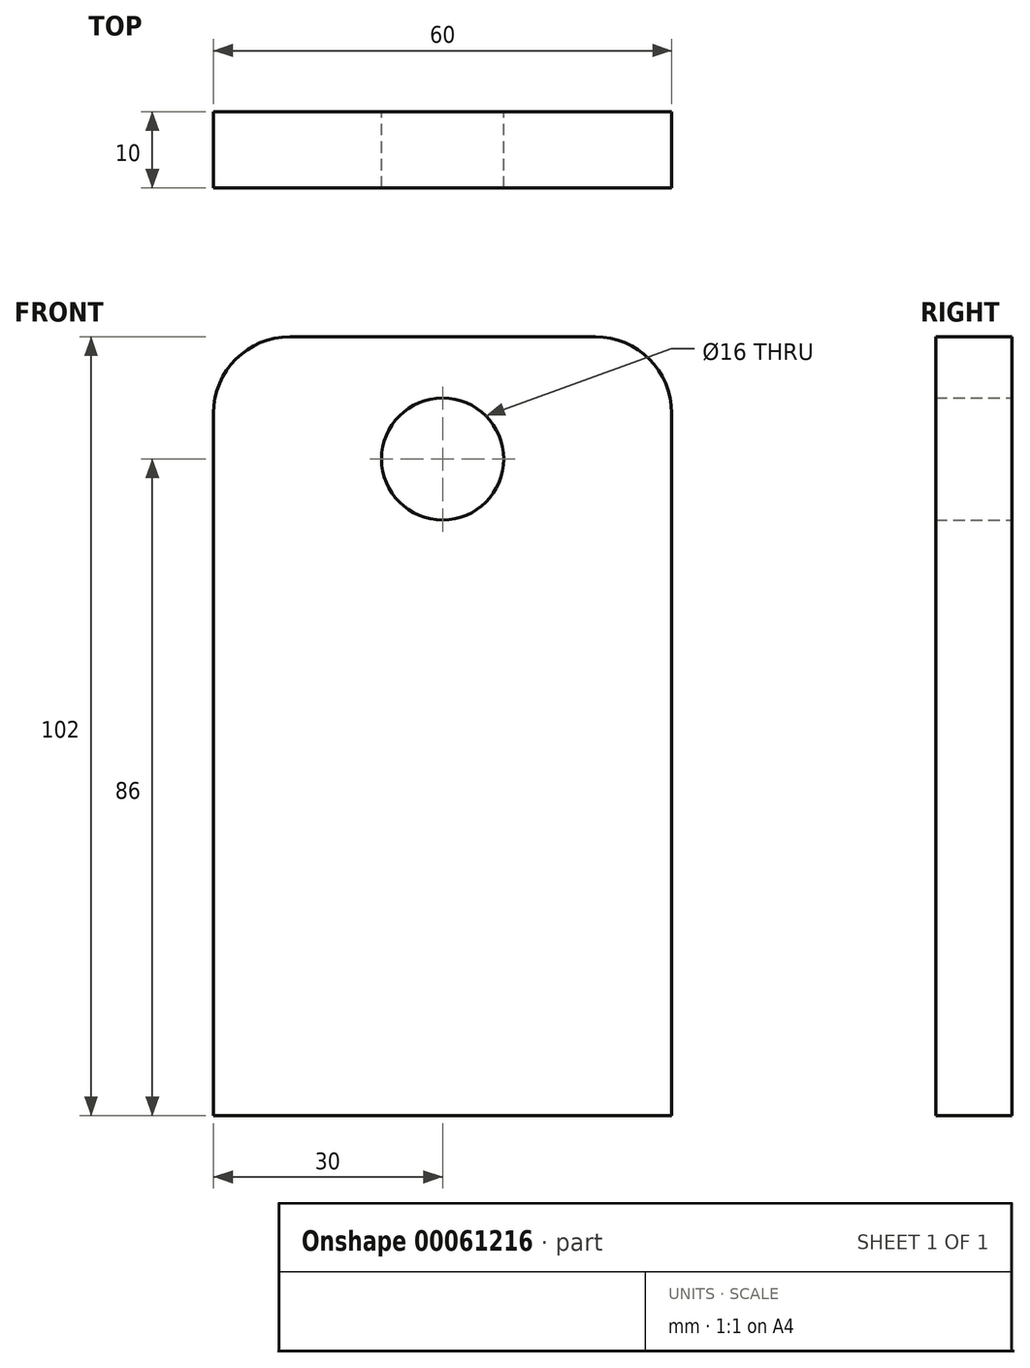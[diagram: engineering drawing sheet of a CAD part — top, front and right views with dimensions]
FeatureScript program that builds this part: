
annotation { "Feature Type Name" : "Feature", "Feature Type Description" : "" }
export const myFeature = defineFeature(function(context is Context, id is Id, definition is map)
    precondition{}
    {
        {
            var Q0;
            Q0=qCreatedBy(makeId("Front.planeOp"),FACE);
            var sketch = newSketch(context, id + "F0", { "sketchPlane" : qUnion([Q0])});
            skLineSegment(sketch, "E0.bottom", {"start": v(0, 0) * mm, "end": v(60, 0) * mm});
            skLineSegment(sketch, "E0.top", {"start": v(10, 102) * mm, "end": v(50, 102) * mm});
            skLineSegment(sketch, "E0.left", {"start": v(0, 0) * mm, "end": v(0, 92) * mm});
            skLineSegment(sketch, "E0.right", {"start": v(60, 0) * mm, "end": v(60, 92) * mm});
            skPoint(sketch, "E1.visualSharp", {"position": v(0, 102) * mm});
            skArc(sketch, "E1.filletArc", {"start": v(10, 102) * mm, "mid": v(2.93, 99.07) * mm, "end": v(0, 92) * mm});
            skPoint(sketch, "E2.visualSharp", {"position": v(60, 102) * mm});
            skArc(sketch, "E2.filletArc", {"start": v(60, 92) * mm, "mid": v(57.07, 99.07) * mm, "end": v(50, 102) * mm});
            skCircle(sketch, "E3", {"center": v(30, 86) * mm, "radius": 8 * mm});
            skPoint(sketch, "E3.centerSnap0", {"position": v(30, 0) * mm});
            skSolve(sketch);
        }
        {
            var Q0;
            Q0=makeQuery(id+"F0.imprint","IMPRINT",FACE,{"disambiguationData":[TD([[makeQuery(id+"F0.imprint","IMPRINT",EDGE,{"derivedFrom":sQuery(id+"F0.wireOp",EDGE,"E0.bottom")}),1.0]])]});
            extrude(context, id + "F1", {"entities" : qUnion([Q0]), "depth" : 10 * mm});
        }
    });
